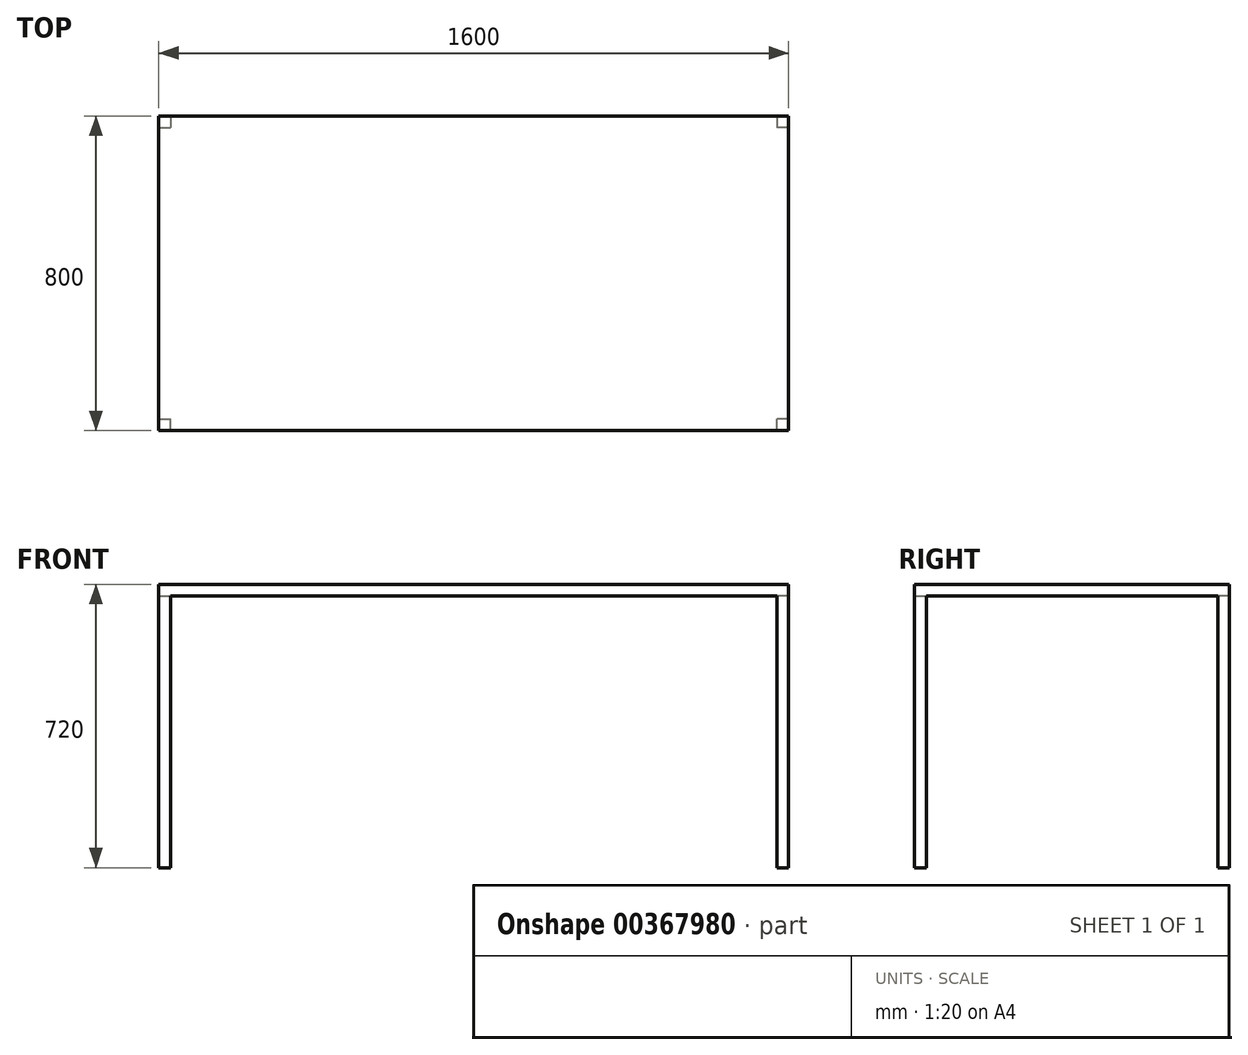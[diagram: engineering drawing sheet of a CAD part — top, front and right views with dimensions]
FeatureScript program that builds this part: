
annotation { "Feature Type Name" : "Feature", "Feature Type Description" : "" }
export const myFeature = defineFeature(function(context is Context, id is Id, definition is map)
    precondition{}
    {
        {
            var Q0;
            Q0=qCreatedBy(makeId("Top.planeOp"),FACE);
            var sketch = newSketch(context, id + "F0", { "sketchPlane" : qUnion([Q0])});
            skLineSegment(sketch, "E0.bottom", {"start": v(0, 0) * mm, "end": v(1600, 0) * mm});
            skLineSegment(sketch, "E0.top", {"start": v(0, 800) * mm, "end": v(1600, 800) * mm});
            skLineSegment(sketch, "E0.left", {"start": v(0, 0) * mm, "end": v(0, 800) * mm});
            skLineSegment(sketch, "E0.right", {"start": v(1600, 0) * mm, "end": v(1600, 800) * mm});
            skSolve(sketch);
        }
        {
            var Q0;
            Q0=makeQuery(id+"F0.imprint","IMPRINT",FACE,{"disambiguationData":[TD([[makeQuery(id+"F0.imprint","IMPRINT",EDGE,{"derivedFrom":sQuery(id+"F0.wireOp",EDGE,"E0.bottom")}),1.0]])]});
            extrude(context, id + "F1", {"entities" : qUnion([Q0]), "depth" : 30 * mm});
        }
        {
            var Q0;
            Q0=qCreatedBy(makeId("Top.planeOp"),FACE);
            var sketch = newSketch(context, id + "F2", { "sketchPlane" : qUnion([Q0])});
            skLineSegment(sketch, "E1.bottom", {"start": v(0, 0) * mm, "end": v(30, 0) * mm});
            skLineSegment(sketch, "E1.top", {"start": v(0, 30) * mm, "end": v(30, 30) * mm});
            skLineSegment(sketch, "E1.left", {"start": v(0, 0) * mm, "end": v(0, 30) * mm});
            skLineSegment(sketch, "E1.right", {"start": v(30, 0) * mm, "end": v(30, 30) * mm});
            skLineSegment(sketch, "E2.bottom", {"start": v(0, 800) * mm, "end": v(30, 800) * mm});
            skLineSegment(sketch, "E2.top", {"start": v(0, 770) * mm, "end": v(30, 770) * mm});
            skLineSegment(sketch, "E2.left", {"start": v(0, 800) * mm, "end": v(0, 770) * mm});
            skLineSegment(sketch, "E2.right", {"start": v(30, 800) * mm, "end": v(30, 770) * mm});
            skLineSegment(sketch, "E3.bottom", {"start": v(1600, 0) * mm, "end": v(1570, 0) * mm});
            skLineSegment(sketch, "E3.top", {"start": v(1600, 30) * mm, "end": v(1570, 30) * mm});
            skLineSegment(sketch, "E3.left", {"start": v(1600, 0) * mm, "end": v(1600, 30) * mm});
            skLineSegment(sketch, "E3.right", {"start": v(1570, 0) * mm, "end": v(1570, 30) * mm});
            skLineSegment(sketch, "E4.bottom", {"start": v(1600, 800) * mm, "end": v(1570, 800) * mm});
            skLineSegment(sketch, "E4.top", {"start": v(1600, 770) * mm, "end": v(1570, 770) * mm});
            skLineSegment(sketch, "E4.left", {"start": v(1600, 800) * mm, "end": v(1600, 770) * mm});
            skLineSegment(sketch, "E4.right", {"start": v(1570, 800) * mm, "end": v(1570, 770) * mm});
            skSolve(sketch);
        }
        {
            var Q0;
            Q0 = qSketchRegion(id + "F2", true);
            extrude(context, id + "F3", {"entities" : qUnion([Q0]), "operationType" : NewBodyOperationType.ADD, "oppositeDirection" : true, "depth" : 690 * mm});
        }
    });
